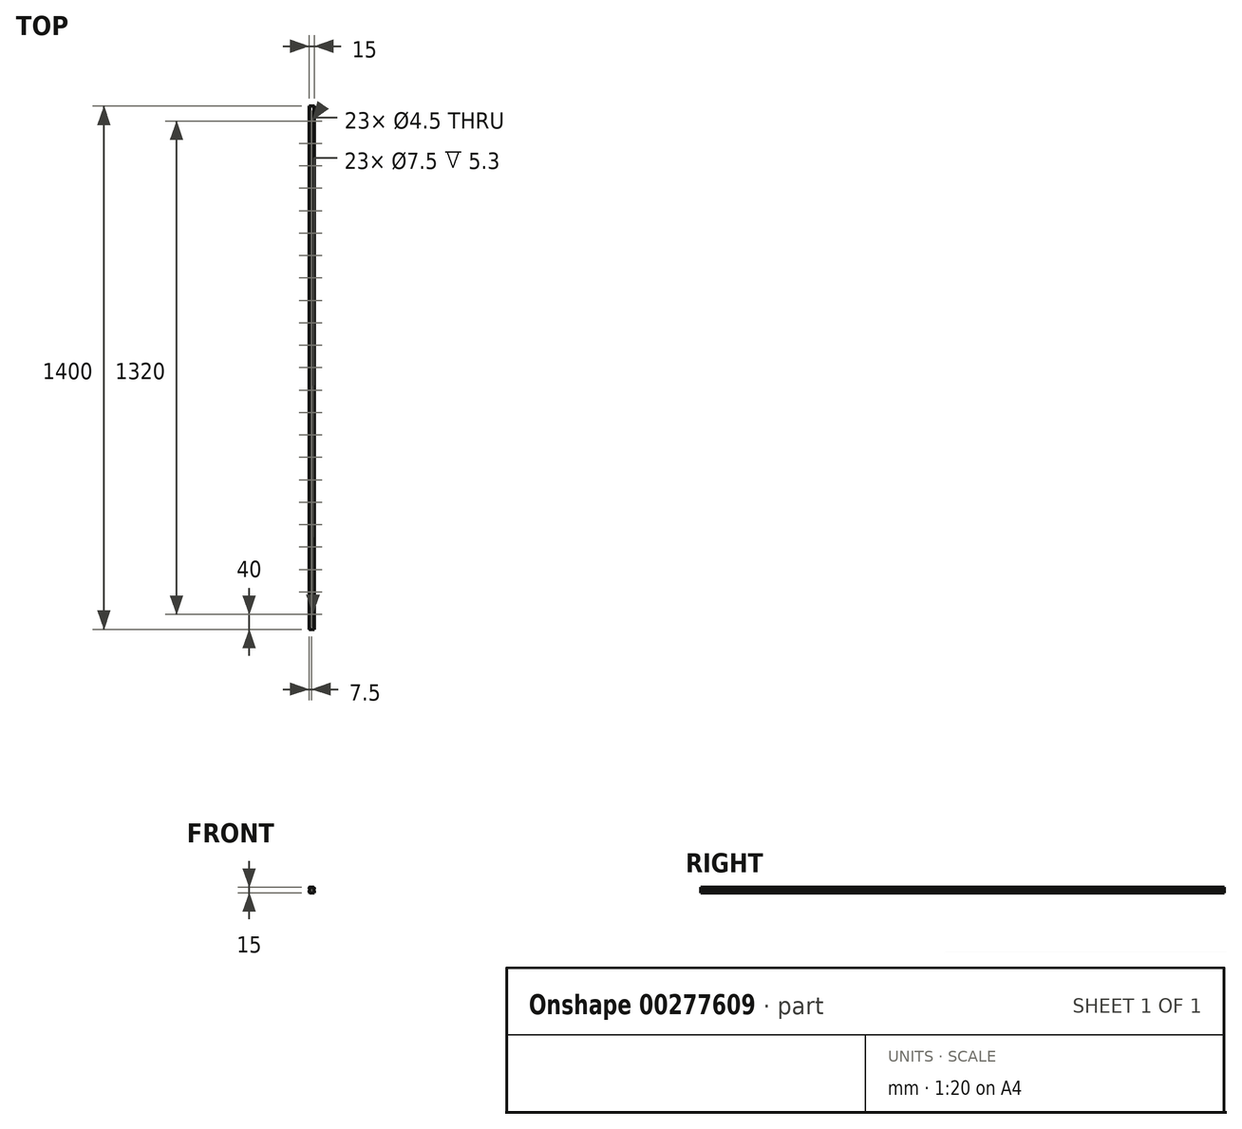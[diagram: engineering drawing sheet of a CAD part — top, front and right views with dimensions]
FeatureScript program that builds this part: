
annotation { "Feature Type Name" : "Feature", "Feature Type Description" : "" }
export const myFeature = defineFeature(function(context is Context, id is Id, definition is map)
    precondition{}
    {
        {
            var Q0;
            Q0=qCreatedBy(makeId("Front.planeOp"),FACE);
            var sketch = newSketch(context, id + "F0", { "sketchPlane" : qUnion([Q0])});
            skLineSegment(sketch, "E0", {"start": v(-6.28, -7.5) * mm, "end": v(6.28, -7.5) * mm});
            skLineSegment(sketch, "E1", {"start": v(7.5, -6.28) * mm, "end": v(7.5, -3.22) * mm});
            skLineSegment(sketch, "E2", {"start": v(5.8, 7.5) * mm, "end": v(-5.8, 7.5) * mm});
            skLineSegment(sketch, "E3", {"start": v(-7.5, 4.94) * mm, "end": v(-7.5, 3.79) * mm});
            skLineSegment(sketch, "E4.0", {"start": v(-7.5, -3.2) * mm, "end": v(7.5, -3.2) * mm, "construction": true});
            skLineSegment(sketch, "E5", {"start": v(-7.49, -3.19) * mm, "end": v(-5.15, -0.85) * mm});
            skLineSegment(sketch, "E6", {"start": v(0, 7.5) * mm, "end": v(0, -7.5) * mm, "construction": true});
            skLineSegment(sketch, "E7", {"start": v(-5.15, -0.85) * mm, "end": v(-5.15, 1.15) * mm});
            skLineSegment(sketch, "E8", {"start": v(-5.15, 1.15) * mm, "end": v(-6.2, 2.2) * mm});
            skLineSegment(sketch, "E9", {"start": v(-6.22, 2.23) * mm, "end": v(-6.22, 2.76) * mm});
            skLineSegment(sketch, "E10.0", {"start": v(-7.08, 5.37) * mm, "end": v(-6.82, 5.37) * mm});
            skLineSegment(sketch, "E11", {"start": v(-6.82, 5.37) * mm, "end": v(-6.22, 5.97) * mm});
            skLineSegment(sketch, "E12.MirrorCS", {"start": v(-6.82, 3.37) * mm, "end": v(-6.22, 2.76) * mm});
            skPoint(sketch, "E13.orphan", {"position": v(-6.22, 5.97) * mm});
            skLineSegment(sketch, "E14.trimOffspring", {"start": v(-6.22, 5.97) * mm, "end": v(-6.22, 7.06) * mm});
            skLineSegment(sketch, "E15", {"start": v(-6.82, 3.37) * mm, "end": v(-7.08, 3.37) * mm});
            skLineSegment(sketch, "E16.trimOffspring", {"start": v(-7.5, -3.22) * mm, "end": v(-7.5, -6.28) * mm});
            skPoint(sketch, "E17.orphan", {"position": v(-7.5, 7.5) * mm});
            skLineSegment(sketch, "E18", {"start": v(-6.22, 5.97) * mm, "end": v(-6.22, 2.76) * mm, "construction": true});
            skLineSegment(sketch, "E19", {"start": v(-6.82, 3.37) * mm, "end": v(-6.22, 3.37) * mm, "construction": true});
            skLineSegment(sketch, "E20", {"start": v(-6.82, 5.37) * mm, "end": v(-6.22, 5.37) * mm, "construction": true});
            skLineSegment(sketch, "E21", {"start": v(-7.49, 4.98) * mm, "end": v(-7.11, 5.35) * mm});
            skLineSegment(sketch, "E22.MirrorCS", {"start": v(-7.49, 3.75) * mm, "end": v(-7.11, 3.38) * mm});
            skPoint(sketch, "E23.orphan", {"position": v(-7.5, 5.37) * mm});
            skPoint(sketch, "E24.orphan", {"position": v(-7.5, 3.37) * mm});
            skLineSegment(sketch, "E25.MirrorCS", {"start": v(7.49, -3.19) * mm, "end": v(5.15, -0.85) * mm});
            skLineSegment(sketch, "E26.MirrorCS", {"start": v(5.15, -0.85) * mm, "end": v(5.15, 1.15) * mm});
            skLineSegment(sketch, "E27.MirrorCS", {"start": v(5.15, 1.15) * mm, "end": v(6.2, 2.2) * mm});
            skLineSegment(sketch, "E28.MirrorCS", {"start": v(6.22, 2.23) * mm, "end": v(6.22, 2.76) * mm});
            skLineSegment(sketch, "E29.MirrorCS", {"start": v(6.82, 3.37) * mm, "end": v(6.22, 2.76) * mm});
            skLineSegment(sketch, "E30.MirrorCS", {"start": v(6.82, 3.37) * mm, "end": v(7.08, 3.37) * mm});
            skLineSegment(sketch, "E31.MirrorCS", {"start": v(7.49, 3.75) * mm, "end": v(7.11, 3.38) * mm});
            skLineSegment(sketch, "E32.MirrorCS", {"start": v(7.5, 4.94) * mm, "end": v(7.5, 3.79) * mm});
            skLineSegment(sketch, "E33.MirrorCS", {"start": v(7.49, 4.98) * mm, "end": v(7.11, 5.35) * mm});
            skLineSegment(sketch, "E34.MirrorCS", {"start": v(7.08, 5.37) * mm, "end": v(6.82, 5.37) * mm});
            skLineSegment(sketch, "E35.MirrorCS", {"start": v(6.82, 5.37) * mm, "end": v(6.22, 5.97) * mm});
            skLineSegment(sketch, "E36.MirrorCS", {"start": v(6.22, 5.97) * mm, "end": v(6.22, 7.06) * mm});
            skPoint(sketch, "E37.orphan", {"position": v(7.5, 7.5) * mm});
            skLineSegment(sketch, "E38.trimOffspring", {"start": v(7.5, 3.77) * mm, "end": v(7.5, 4.97) * mm});
            skLineSegment(sketch, "E39", {"start": v(-7.49, -6.31) * mm, "end": v(-6.31, -7.49) * mm});
            skPoint(sketch, "E40.orphan", {"position": v(-7.5, -7.5) * mm});
            skLineSegment(sketch, "E41.MirrorCS", {"start": v(7.49, -6.31) * mm, "end": v(6.31, -7.49) * mm});
            skPoint(sketch, "E42.orphan", {"position": v(7.5, -7.5) * mm});
            skPoint(sketch, "E43", {"position": v(0, 0) * mm});
            skLineSegment(sketch, "E44", {"start": v(6.82, 5.37) * mm, "end": v(-6.82, 5.37) * mm, "construction": true});
            skLineSegment(sketch, "E45", {"start": v(6.82, 3.37) * mm, "end": v(-6.82, 3.37) * mm, "construction": true});
            skPoint(sketch, "E46.start.orphan", {"position": v(-7.5, 4.37) * mm});
            skLineSegment(sketch, "E47", {"start": v(-6.2, 7.1) * mm, "end": v(-5.83, 7.48) * mm});
            skLineSegment(sketch, "E48.MirrorCS", {"start": v(6.2, 7.1) * mm, "end": v(5.83, 7.48) * mm});
            skPoint(sketch, "E49.orphan", {"position": v(-6.22, 7.5) * mm});
            skPoint(sketch, "E50.orphan", {"position": v(6.22, 7.5) * mm});
            skPoint(sketch, "E51.visualSharp", {"position": v(-5.82, 7.5) * mm});
            skArc(sketch, "E51.filletArc", {"start": v(-5.8, 7.5) * mm, "mid": v(-5.81, 7.5) * mm, "end": v(-5.83, 7.48) * mm});
            skPoint(sketch, "E52.visualSharp", {"position": v(-6.22, 7.08) * mm});
            skArc(sketch, "E52.filletArc", {"start": v(-6.2, 7.1) * mm, "mid": v(-6.21, 7.08) * mm, "end": v(-6.22, 7.06) * mm});
            skPoint(sketch, "E53.visualSharp", {"position": v(-7.1, 5.37) * mm});
            skArc(sketch, "E53.filletArc", {"start": v(-7.08, 5.37) * mm, "mid": v(-7.1, 5.36) * mm, "end": v(-7.11, 5.35) * mm});
            skPoint(sketch, "E54.visualSharp", {"position": v(-7.5, 4.97) * mm});
            skArc(sketch, "E54.filletArc", {"start": v(-7.49, 4.98) * mm, "mid": v(-7.5, 4.96) * mm, "end": v(-7.5, 4.94) * mm});
            skPoint(sketch, "E55.visualSharp", {"position": v(-7.5, 3.77) * mm});
            skArc(sketch, "E55.filletArc", {"start": v(-7.5, 3.79) * mm, "mid": v(-7.5, 3.77) * mm, "end": v(-7.49, 3.75) * mm});
            skPoint(sketch, "E56.visualSharp", {"position": v(-7.1, 3.37) * mm});
            skArc(sketch, "E56.filletArc", {"start": v(-7.11, 3.38) * mm, "mid": v(-7.1, 3.37) * mm, "end": v(-7.08, 3.37) * mm});
            skPoint(sketch, "E57.visualSharp", {"position": v(-6.22, 2.2) * mm});
            skArc(sketch, "E57.filletArc", {"start": v(-6.22, 2.23) * mm, "mid": v(-6.21, 2.2) * mm, "end": v(-6.2, 2.2) * mm});
            skPoint(sketch, "E58.visualSharp", {"position": v(-7.5, -3.2) * mm});
            skArc(sketch, "E58.filletArc", {"start": v(-7.49, -3.19) * mm, "mid": v(-7.5, -3.2) * mm, "end": v(-7.5, -3.22) * mm});
            skPoint(sketch, "E59.visualSharp", {"position": v(-7.5, -6.3) * mm});
            skArc(sketch, "E59.filletArc", {"start": v(-7.5, -6.28) * mm, "mid": v(-7.5, -6.3) * mm, "end": v(-7.49, -6.31) * mm});
            skPoint(sketch, "E60.visualSharp", {"position": v(-6.3, -7.5) * mm});
            skArc(sketch, "E60.filletArc", {"start": v(-6.31, -7.49) * mm, "mid": v(-6.3, -7.5) * mm, "end": v(-6.28, -7.5) * mm});
            skPoint(sketch, "E61.visualSharp", {"position": v(6.3, -7.5) * mm});
            skArc(sketch, "E61.filletArc", {"start": v(6.28, -7.5) * mm, "mid": v(6.3, -7.5) * mm, "end": v(6.31, -7.49) * mm});
            skPoint(sketch, "E62.visualSharp", {"position": v(7.5, -6.3) * mm});
            skArc(sketch, "E62.filletArc", {"start": v(7.49, -6.31) * mm, "mid": v(7.5, -6.3) * mm, "end": v(7.5, -6.28) * mm});
            skPoint(sketch, "E63.visualSharp", {"position": v(7.5, -3.2) * mm});
            skArc(sketch, "E63.filletArc", {"start": v(7.5, -3.22) * mm, "mid": v(7.5, -3.2) * mm, "end": v(7.49, -3.19) * mm});
            skPoint(sketch, "E64.visualSharp", {"position": v(6.22, 2.2) * mm});
            skArc(sketch, "E64.filletArc", {"start": v(6.2, 2.2) * mm, "mid": v(6.21, 2.2) * mm, "end": v(6.22, 2.23) * mm});
            skPoint(sketch, "E65.visualSharp", {"position": v(7.1, 3.37) * mm});
            skArc(sketch, "E65.filletArc", {"start": v(7.08, 3.37) * mm, "mid": v(7.1, 3.37) * mm, "end": v(7.11, 3.38) * mm});
            skPoint(sketch, "E66.visualSharp", {"position": v(7.5, 3.77) * mm});
            skArc(sketch, "E66.filletArc", {"start": v(7.49, 3.75) * mm, "mid": v(7.5, 3.77) * mm, "end": v(7.5, 3.79) * mm});
            skPoint(sketch, "E67.visualSharp", {"position": v(7.5, 4.97) * mm});
            skArc(sketch, "E67.filletArc", {"start": v(7.5, 4.94) * mm, "mid": v(7.5, 4.96) * mm, "end": v(7.49, 4.98) * mm});
            skPoint(sketch, "E68.visualSharp", {"position": v(7.1, 5.37) * mm});
            skArc(sketch, "E68.filletArc", {"start": v(7.11, 5.35) * mm, "mid": v(7.1, 5.36) * mm, "end": v(7.08, 5.37) * mm});
            skPoint(sketch, "E69.visualSharp", {"position": v(6.22, 7.08) * mm});
            skArc(sketch, "E69.filletArc", {"start": v(6.22, 7.06) * mm, "mid": v(6.21, 7.08) * mm, "end": v(6.2, 7.1) * mm});
            skPoint(sketch, "E70.visualSharp", {"position": v(5.82, 7.5) * mm});
            skArc(sketch, "E70.filletArc", {"start": v(5.83, 7.48) * mm, "mid": v(5.81, 7.5) * mm, "end": v(5.8, 7.5) * mm});
            skSolve(sketch);
        }
        {
            var Q0;
            Q0=makeQuery(id+"F0.imprint","IMPRINT",FACE,{"disambiguationData":[TD([[makeQuery(id+"F0.imprint","IMPRINT",EDGE,{"derivedFrom":sQuery(id+"F0.wireOp",EDGE,"E0")}),1.0]])]});
            extrude(context, id + "F1", {"entities" : qUnion([Q0]), "endBound" : BoundingType.SYMMETRIC, "depth" : 1400 * mm});
        }
        {
            var Q0;
            Q0=makeQuery(id+"F1.opExtrude","SWEPT_FACE",FACE,{"disambiguationData":[OSD([sQuery(id+"F0.wireOp",EDGE,"E2")])]});
            var sketch = newSketch(context, id + "F2", { "sketchPlane" : qUnion([Q0])});
            skPoint(sketch, "E71.endSnap0", {"position": v(0, -700) * mm});
            skCircle(sketch, "E72", {"center": v(0, -660) * mm, "radius": 2.25 * mm});
            skCircle(sketch, "E73", {"center": v(0, -660) * mm, "radius": 3.75 * mm});
            skCircle(sketch, "E74.0.1.0", {"center": v(0, -600) * mm, "radius": 3.75 * mm});
            skCircle(sketch, "E74.0.1.1", {"center": v(0, -600) * mm, "radius": 2.25 * mm});
            skCircle(sketch, "E74.0.2.0", {"center": v(0, -540) * mm, "radius": 3.75 * mm});
            skCircle(sketch, "E74.0.2.1", {"center": v(0, -540) * mm, "radius": 2.25 * mm});
            skCircle(sketch, "E74.0.3.0", {"center": v(0, -480) * mm, "radius": 3.75 * mm});
            skCircle(sketch, "E74.0.3.1", {"center": v(0, -480) * mm, "radius": 2.25 * mm});
            skCircle(sketch, "E74.0.4.0", {"center": v(0, -420) * mm, "radius": 3.75 * mm});
            skCircle(sketch, "E74.0.4.1", {"center": v(0, -420) * mm, "radius": 2.25 * mm});
            skCircle(sketch, "E74.0.5.0", {"center": v(0, -360) * mm, "radius": 3.75 * mm});
            skCircle(sketch, "E74.0.5.1", {"center": v(0, -360) * mm, "radius": 2.25 * mm});
            skCircle(sketch, "E74.0.6.0", {"center": v(0, -300) * mm, "radius": 3.75 * mm});
            skCircle(sketch, "E74.0.6.1", {"center": v(0, -300) * mm, "radius": 2.25 * mm});
            skCircle(sketch, "E74.0.7.0", {"center": v(0, -240) * mm, "radius": 3.75 * mm});
            skCircle(sketch, "E74.0.7.1", {"center": v(0, -240) * mm, "radius": 2.25 * mm});
            skCircle(sketch, "E74.0.8.0", {"center": v(0, -180) * mm, "radius": 3.75 * mm});
            skCircle(sketch, "E74.0.8.1", {"center": v(0, -180) * mm, "radius": 2.25 * mm});
            skCircle(sketch, "E74.0.9.0", {"center": v(0, -120) * mm, "radius": 3.75 * mm});
            skCircle(sketch, "E74.0.9.1", {"center": v(0, -120) * mm, "radius": 2.25 * mm});
            skCircle(sketch, "E74.0.10.0", {"center": v(0, -60) * mm, "radius": 3.75 * mm});
            skCircle(sketch, "E74.0.10.1", {"center": v(0, -60) * mm, "radius": 2.25 * mm});
            skCircle(sketch, "E74.0.11.0", {"center": v(0, 0) * mm, "radius": 3.75 * mm});
            skCircle(sketch, "E74.0.11.1", {"center": v(0, 0) * mm, "radius": 2.25 * mm});
            skCircle(sketch, "E74.0.12.0", {"center": v(0, 60) * mm, "radius": 3.75 * mm});
            skCircle(sketch, "E74.0.12.1", {"center": v(0, 60) * mm, "radius": 2.25 * mm});
            skCircle(sketch, "E74.0.13.0", {"center": v(0, 120) * mm, "radius": 3.75 * mm});
            skCircle(sketch, "E74.0.13.1", {"center": v(0, 120) * mm, "radius": 2.25 * mm});
            skCircle(sketch, "E74.0.14.0", {"center": v(0, 180) * mm, "radius": 3.75 * mm});
            skCircle(sketch, "E74.0.14.1", {"center": v(0, 180) * mm, "radius": 2.25 * mm});
            skCircle(sketch, "E74.0.15.0", {"center": v(0, 240) * mm, "radius": 3.75 * mm});
            skCircle(sketch, "E74.0.15.1", {"center": v(0, 240) * mm, "radius": 2.25 * mm});
            skCircle(sketch, "E74.0.16.0", {"center": v(0, 300) * mm, "radius": 3.75 * mm});
            skCircle(sketch, "E74.0.16.1", {"center": v(0, 300) * mm, "radius": 2.25 * mm});
            skCircle(sketch, "E74.0.17.0", {"center": v(0, 360) * mm, "radius": 3.75 * mm});
            skCircle(sketch, "E74.0.17.1", {"center": v(0, 360) * mm, "radius": 2.25 * mm});
            skCircle(sketch, "E74.0.18.0", {"center": v(0, 420) * mm, "radius": 3.75 * mm});
            skCircle(sketch, "E74.0.18.1", {"center": v(0, 420) * mm, "radius": 2.25 * mm});
            skCircle(sketch, "E74.0.19.0", {"center": v(0, 480) * mm, "radius": 3.75 * mm});
            skCircle(sketch, "E74.0.19.1", {"center": v(0, 480) * mm, "radius": 2.25 * mm});
            skCircle(sketch, "E74.0.20.0", {"center": v(0, 540) * mm, "radius": 3.75 * mm});
            skCircle(sketch, "E74.0.20.1", {"center": v(0, 540) * mm, "radius": 2.25 * mm});
            skCircle(sketch, "E74.0.21.0", {"center": v(0, 600) * mm, "radius": 3.75 * mm});
            skCircle(sketch, "E74.0.21.1", {"center": v(0, 600) * mm, "radius": 2.25 * mm});
            skCircle(sketch, "E74.0.22.0", {"center": v(0, 660) * mm, "radius": 3.75 * mm});
            skCircle(sketch, "E74.0.22.1", {"center": v(0, 660) * mm, "radius": 2.25 * mm});
            skLineSegment(sketch, "E74.direction1", {"start": v(0, -660) * mm, "end": v(25, -660) * mm, "construction": true});
            skLineSegment(sketch, "E74.direction2", {"start": v(0, -660) * mm, "end": v(0, -600) * mm, "construction": true});
            skSolve(sketch);
        }
        {
            var Q0;
            Q0=makeQuery(id+"F2.imprint","IMPRINT",FACE,{"disambiguationData":[TD([[makeQuery(id+"F2.imprint","IMPRINT",EDGE,{"derivedFrom":sQuery(id+"F2.wireOp",EDGE,"E74.0.1.1")}),1.0]])]});
            var Q1;
            Q1=makeQuery(id+"F2.imprint","IMPRINT",FACE,{"disambiguationData":[TD([[makeQuery(id+"F2.imprint","IMPRINT",EDGE,{"derivedFrom":sQuery(id+"F2.wireOp",EDGE,"E74.0.2.1")}),1.0]])]});
            var Q2;
            Q2=makeQuery(id+"F2.imprint","IMPRINT",FACE,{"disambiguationData":[TD([[makeQuery(id+"F2.imprint","IMPRINT",EDGE,{"derivedFrom":sQuery(id+"F2.wireOp",EDGE,"E74.0.3.1")}),1.0]])]});
            var Q3;
            Q3=makeQuery(id+"F2.imprint","IMPRINT",FACE,{"disambiguationData":[TD([[makeQuery(id+"F2.imprint","IMPRINT",EDGE,{"derivedFrom":sQuery(id+"F2.wireOp",EDGE,"E74.0.4.1")}),1.0]])]});
            var Q4;
            Q4=makeQuery(id+"F2.imprint","IMPRINT",FACE,{"disambiguationData":[TD([[makeQuery(id+"F2.imprint","IMPRINT",EDGE,{"derivedFrom":sQuery(id+"F2.wireOp",EDGE,"E74.0.5.1")}),1.0]])]});
            var Q5;
            Q5=makeQuery(id+"F2.imprint","IMPRINT",FACE,{"disambiguationData":[TD([[makeQuery(id+"F2.imprint","IMPRINT",EDGE,{"derivedFrom":sQuery(id+"F2.wireOp",EDGE,"E74.0.6.1")}),1.0]])]});
            var Q6;
            Q6=makeQuery(id+"F2.imprint","IMPRINT",FACE,{"disambiguationData":[TD([[makeQuery(id+"F2.imprint","IMPRINT",EDGE,{"derivedFrom":sQuery(id+"F2.wireOp",EDGE,"E74.0.7.1")}),1.0]])]});
            var Q7;
            Q7=makeQuery(id+"F2.imprint","IMPRINT",FACE,{"disambiguationData":[TD([[makeQuery(id+"F2.imprint","IMPRINT",EDGE,{"derivedFrom":sQuery(id+"F2.wireOp",EDGE,"E74.0.8.1")}),1.0]])]});
            var Q8;
            Q8=makeQuery(id+"F2.imprint","IMPRINT",FACE,{"disambiguationData":[TD([[makeQuery(id+"F2.imprint","IMPRINT",EDGE,{"derivedFrom":sQuery(id+"F2.wireOp",EDGE,"E74.0.9.1")}),1.0]])]});
            var Q9;
            Q9=makeQuery(id+"F2.imprint","IMPRINT",FACE,{"disambiguationData":[TD([[makeQuery(id+"F2.imprint","IMPRINT",EDGE,{"derivedFrom":sQuery(id+"F2.wireOp",EDGE,"E74.0.10.1")}),1.0]])]});
            var Q10;
            Q10=makeQuery(id+"F2.imprint","IMPRINT",FACE,{"disambiguationData":[TD([[makeQuery(id+"F2.imprint","IMPRINT",EDGE,{"derivedFrom":sQuery(id+"F2.wireOp",EDGE,"E74.0.11.1")}),1.0]])]});
            var Q11;
            Q11=makeQuery(id+"F2.imprint","IMPRINT",FACE,{"disambiguationData":[TD([[makeQuery(id+"F2.imprint","IMPRINT",EDGE,{"derivedFrom":sQuery(id+"F2.wireOp",EDGE,"E74.0.12.1")}),1.0]])]});
            var Q12;
            Q12=makeQuery(id+"F2.imprint","IMPRINT",FACE,{"disambiguationData":[TD([[makeQuery(id+"F2.imprint","IMPRINT",EDGE,{"derivedFrom":sQuery(id+"F2.wireOp",EDGE,"E74.0.14.1")}),1.0]])]});
            var Q13;
            Q13=makeQuery(id+"F2.imprint","IMPRINT",FACE,{"disambiguationData":[TD([[makeQuery(id+"F2.imprint","IMPRINT",EDGE,{"derivedFrom":sQuery(id+"F2.wireOp",EDGE,"E74.0.13.1")}),1.0]])]});
            var Q14;
            Q14=makeQuery(id+"F2.imprint","IMPRINT",FACE,{"disambiguationData":[TD([[makeQuery(id+"F2.imprint","IMPRINT",EDGE,{"derivedFrom":sQuery(id+"F2.wireOp",EDGE,"E74.0.16.1")}),1.0]])]});
            var Q15;
            Q15=makeQuery(id+"F2.imprint","IMPRINT",FACE,{"disambiguationData":[TD([[makeQuery(id+"F2.imprint","IMPRINT",EDGE,{"derivedFrom":sQuery(id+"F2.wireOp",EDGE,"E74.0.15.1")}),1.0]])]});
            var Q16;
            Q16=makeQuery(id+"F2.imprint","IMPRINT",FACE,{"disambiguationData":[TD([[makeQuery(id+"F2.imprint","IMPRINT",EDGE,{"derivedFrom":sQuery(id+"F2.wireOp",EDGE,"E74.0.17.1")}),1.0]])]});
            var Q17;
            Q17=makeQuery(id+"F2.imprint","IMPRINT",FACE,{"disambiguationData":[TD([[makeQuery(id+"F2.imprint","IMPRINT",EDGE,{"derivedFrom":sQuery(id+"F2.wireOp",EDGE,"E74.0.18.1")}),1.0]])]});
            var Q18;
            Q18=makeQuery(id+"F2.imprint","IMPRINT",FACE,{"disambiguationData":[TD([[makeQuery(id+"F2.imprint","IMPRINT",EDGE,{"derivedFrom":sQuery(id+"F2.wireOp",EDGE,"E74.0.19.1")}),1.0]])]});
            var Q19;
            Q19=makeQuery(id+"F2.imprint","IMPRINT",FACE,{"disambiguationData":[TD([[makeQuery(id+"F2.imprint","IMPRINT",EDGE,{"derivedFrom":sQuery(id+"F2.wireOp",EDGE,"E74.0.22.1")}),1.0]])]});
            var Q20;
            Q20=makeQuery(id+"F2.imprint","IMPRINT",FACE,{"disambiguationData":[TD([[makeQuery(id+"F2.imprint","IMPRINT",EDGE,{"derivedFrom":sQuery(id+"F2.wireOp",EDGE,"E74.0.21.1")}),1.0]])]});
            var Q21;
            Q21=makeQuery(id+"F2.imprint","IMPRINT",FACE,{"disambiguationData":[TD([[makeQuery(id+"F2.imprint","IMPRINT",EDGE,{"derivedFrom":sQuery(id+"F2.wireOp",EDGE,"E74.0.20.1")}),1.0]])]});
            var Q22;
            Q22=makeQuery(id+"F2.imprint","IMPRINT",FACE,{"disambiguationData":[TD([[makeQuery(id+"F2.imprint","IMPRINT",EDGE,{"derivedFrom":sQuery(id+"F2.wireOp",EDGE,"E72")}),1.0]])]});
            extrude(context, id + "F3", {"entities" : qUnion([Q0, Q1, Q2, Q3, Q4, Q5, Q6, Q7, Q8, Q9, Q10, Q11, Q12, Q13, Q14, Q15, Q16, Q17, Q18, Q19, Q20, Q21, Q22]), "operationType" : NewBodyOperationType.REMOVE, "oppositeDirection" : true, "depth" : 25 * mm});
        }
        {
            var Q0;
            Q0=makeQuery(id+"F2.imprint","IMPRINT",FACE,{"disambiguationData":[TD([[makeQuery(id+"F2.imprint","IMPRINT",EDGE,{"derivedFrom":sQuery(id+"F2.wireOp",EDGE,"E72")}),-1.0]])]});
            var Q1;
            Q1=makeQuery(id+"F2.imprint","IMPRINT",FACE,{"disambiguationData":[TD([[makeQuery(id+"F2.imprint","IMPRINT",EDGE,{"derivedFrom":sQuery(id+"F2.wireOp",EDGE,"E74.0.1.0")}),1.0]])]});
            var Q2;
            Q2=makeQuery(id+"F2.imprint","IMPRINT",FACE,{"disambiguationData":[TD([[makeQuery(id+"F2.imprint","IMPRINT",EDGE,{"derivedFrom":sQuery(id+"F2.wireOp",EDGE,"E74.0.2.0")}),1.0]])]});
            var Q3;
            Q3=makeQuery(id+"F2.imprint","IMPRINT",FACE,{"disambiguationData":[TD([[makeQuery(id+"F2.imprint","IMPRINT",EDGE,{"derivedFrom":sQuery(id+"F2.wireOp",EDGE,"E74.0.4.0")}),1.0]])]});
            var Q4;
            Q4=makeQuery(id+"F2.imprint","IMPRINT",FACE,{"disambiguationData":[TD([[makeQuery(id+"F2.imprint","IMPRINT",EDGE,{"derivedFrom":sQuery(id+"F2.wireOp",EDGE,"E74.0.3.0")}),1.0]])]});
            var Q5;
            Q5=makeQuery(id+"F2.imprint","IMPRINT",FACE,{"disambiguationData":[TD([[makeQuery(id+"F2.imprint","IMPRINT",EDGE,{"derivedFrom":sQuery(id+"F2.wireOp",EDGE,"E74.0.5.0")}),1.0]])]});
            var Q6;
            Q6=makeQuery(id+"F2.imprint","IMPRINT",FACE,{"disambiguationData":[TD([[makeQuery(id+"F2.imprint","IMPRINT",EDGE,{"derivedFrom":sQuery(id+"F2.wireOp",EDGE,"E74.0.6.0")}),1.0]])]});
            var Q7;
            Q7=makeQuery(id+"F2.imprint","IMPRINT",FACE,{"disambiguationData":[TD([[makeQuery(id+"F2.imprint","IMPRINT",EDGE,{"derivedFrom":sQuery(id+"F2.wireOp",EDGE,"E74.0.7.0")}),1.0]])]});
            var Q8;
            Q8=makeQuery(id+"F2.imprint","IMPRINT",FACE,{"disambiguationData":[TD([[makeQuery(id+"F2.imprint","IMPRINT",EDGE,{"derivedFrom":sQuery(id+"F2.wireOp",EDGE,"E74.0.8.0")}),1.0]])]});
            var Q9;
            Q9=makeQuery(id+"F2.imprint","IMPRINT",FACE,{"disambiguationData":[TD([[makeQuery(id+"F2.imprint","IMPRINT",EDGE,{"derivedFrom":sQuery(id+"F2.wireOp",EDGE,"E74.0.9.0")}),1.0]])]});
            var Q10;
            Q10=makeQuery(id+"F2.imprint","IMPRINT",FACE,{"disambiguationData":[TD([[makeQuery(id+"F2.imprint","IMPRINT",EDGE,{"derivedFrom":sQuery(id+"F2.wireOp",EDGE,"E74.0.10.0")}),1.0]])]});
            var Q11;
            Q11=makeQuery(id+"F2.imprint","IMPRINT",FACE,{"disambiguationData":[TD([[makeQuery(id+"F2.imprint","IMPRINT",EDGE,{"derivedFrom":sQuery(id+"F2.wireOp",EDGE,"E74.0.11.0")}),1.0]])]});
            var Q12;
            Q12=makeQuery(id+"F2.imprint","IMPRINT",FACE,{"disambiguationData":[TD([[makeQuery(id+"F2.imprint","IMPRINT",EDGE,{"derivedFrom":sQuery(id+"F2.wireOp",EDGE,"E74.0.12.0")}),1.0]])]});
            var Q13;
            Q13=makeQuery(id+"F2.imprint","IMPRINT",FACE,{"disambiguationData":[TD([[makeQuery(id+"F2.imprint","IMPRINT",EDGE,{"derivedFrom":sQuery(id+"F2.wireOp",EDGE,"E74.0.13.0")}),1.0]])]});
            var Q14;
            Q14=makeQuery(id+"F2.imprint","IMPRINT",FACE,{"disambiguationData":[TD([[makeQuery(id+"F2.imprint","IMPRINT",EDGE,{"derivedFrom":sQuery(id+"F2.wireOp",EDGE,"E74.0.14.0")}),1.0]])]});
            var Q15;
            Q15=makeQuery(id+"F2.imprint","IMPRINT",FACE,{"disambiguationData":[TD([[makeQuery(id+"F2.imprint","IMPRINT",EDGE,{"derivedFrom":sQuery(id+"F2.wireOp",EDGE,"E74.0.15.0")}),1.0]])]});
            var Q16;
            Q16=makeQuery(id+"F2.imprint","IMPRINT",FACE,{"disambiguationData":[TD([[makeQuery(id+"F2.imprint","IMPRINT",EDGE,{"derivedFrom":sQuery(id+"F2.wireOp",EDGE,"E74.0.17.0")}),1.0]])]});
            var Q17;
            Q17=makeQuery(id+"F2.imprint","IMPRINT",FACE,{"disambiguationData":[TD([[makeQuery(id+"F2.imprint","IMPRINT",EDGE,{"derivedFrom":sQuery(id+"F2.wireOp",EDGE,"E74.0.16.0")}),1.0]])]});
            var Q18;
            Q18=makeQuery(id+"F2.imprint","IMPRINT",FACE,{"disambiguationData":[TD([[makeQuery(id+"F2.imprint","IMPRINT",EDGE,{"derivedFrom":sQuery(id+"F2.wireOp",EDGE,"E74.0.18.0")}),1.0]])]});
            var Q19;
            Q19=makeQuery(id+"F2.imprint","IMPRINT",FACE,{"disambiguationData":[TD([[makeQuery(id+"F2.imprint","IMPRINT",EDGE,{"derivedFrom":sQuery(id+"F2.wireOp",EDGE,"E74.0.19.0")}),1.0]])]});
            var Q20;
            Q20=makeQuery(id+"F2.imprint","IMPRINT",FACE,{"disambiguationData":[TD([[makeQuery(id+"F2.imprint","IMPRINT",EDGE,{"derivedFrom":sQuery(id+"F2.wireOp",EDGE,"E74.0.21.0")}),1.0]])]});
            var Q21;
            Q21=makeQuery(id+"F2.imprint","IMPRINT",FACE,{"disambiguationData":[TD([[makeQuery(id+"F2.imprint","IMPRINT",EDGE,{"derivedFrom":sQuery(id+"F2.wireOp",EDGE,"E74.0.20.0")}),1.0]])]});
            var Q22;
            Q22=makeQuery(id+"F2.imprint","IMPRINT",FACE,{"disambiguationData":[TD([[makeQuery(id+"F2.imprint","IMPRINT",EDGE,{"derivedFrom":sQuery(id+"F2.wireOp",EDGE,"E74.0.22.0")}),1.0]])]});
            extrude(context, id + "F4", {"entities" : qUnion([Q0, Q1, Q2, Q3, Q4, Q5, Q6, Q7, Q8, Q9, Q10, Q11, Q12, Q13, Q14, Q15, Q16, Q17, Q18, Q19, Q20, Q21, Q22]), "operationType" : NewBodyOperationType.REMOVE, "oppositeDirection" : true, "depth" : 5.3 * mm});
        }
    });
